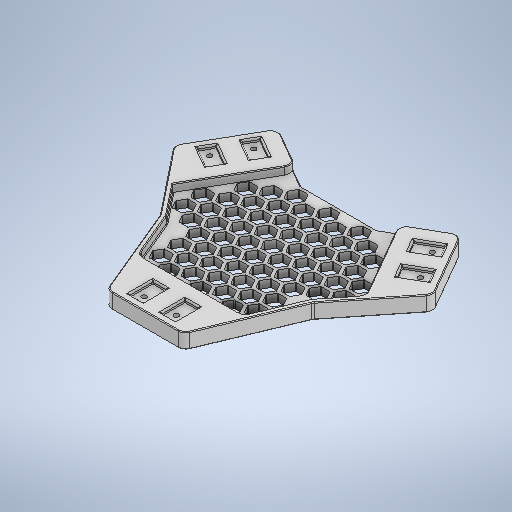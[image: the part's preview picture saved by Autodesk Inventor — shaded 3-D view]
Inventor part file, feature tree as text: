
AUTODESK INVENTOR PART (.ipt)
format: ipt  version: 2025 (Build 290162000, 162)  size: 1,535,488 bytes
history: native  units: in
note: dims shown in document units (in); Inventor stores cm internally (conversion verified against a paired STEP export)
features: extrude x6, fillet x5, sketch x4, projected_geometry x4, other x3, pattern_linear x1
ambient origin geometry x8: Origin, YZ Plane, XZ Plane, XY Plane, X Axis, Y Axis, Z Axis, Center Point
bodies: Solid1 (feature_tree)
feature tree (23):
  extrude  "Extrusion1"  Depth=3.937in
  extrude  "Extrusion2"  Depth=0.1969in
  sketch  "Sketch4"  dims[d4=0.1969in d5=0.0in d6=0.5197in]
  extrude  "Extrusion3"  TaperAngle=120.0deg  [1 undecoded]
  extrude  "Extrusion4"  Depth=1.9685in
  fillet  "Fillet3"  Radius=1.9685in
  fillet  "Fillet4"  Radius=0.1181in
  extrude  "Extrusion5"  Depth=0.0197in
  fillet  "Fillet6"  Radius=0.1969in
  fillet  "Fillet7"  Radius=2.3622in
  extrude  "Extrusion6"  Depth=1.1811in
  other  "Work Axis1"
  other  "Work Axis2"
  other  "Work Axis3"
  pattern_linear  "Rectangular Pattern1"  Spacing1=0.3937in  [1 undecoded]
  fillet  "Fillet8"  Radius=0.3937in
  sketch  "Sketch2"  dims[d2=2.0472in d3=3.937in]
  projected_geometry  "Projected Loop1"
  projected_geometry  "Projected Loop3"
  sketch  "Sketch5"  dims[d7=120.0deg d8=120.0deg]
  projected_geometry  "Projected Loop4"
  sketch  "Sketch6"  dims[d9=3.937in d10=1.9685in d11=1.9685in d12=0.1181in d13=0.1181in d14=0.1969in d15=0.0in d17=2.3622in d19=1.1811in d21=0.3937in d22=0.8327in d23=0.3937in d25=0.126in d26=0.3543in d27=0.5984in d28=0.3543in d29=0.5984in d30=0.3543in d31=0.5984in d32=0.3543in d33=0.5984in d34=0.3543in d35=0.5984in d36=0.3543in d37=0.5984in d38=0.2008in d39=0.2008in d40=0.2008in d41=0.2008in d42=0.2008in d43=0.2008in d44=0.0827in d45=0.0in d46=0.0in d47=0.0in d48=0.0394in d49=0.0197in d51=0.2441in d52=0.1575in d53=0.0in d56=1.9685in d57=0.3937in d58=0.3937in d59=0.1969in d60=0.0197in d61=0.3937in d62=1.0in d63=0.0in d64=4.3307in d66=0.4724in d67=3.937in d69=0.4724in d70=0.0in d71=0.0197in]
  projected_geometry  "Projected Loop5"
note: 2 required parameter values undecoded (feature->parameter linkage not recoverable at this tier; creation-order binding heuristic only, values carry confidence <= 0.55)
